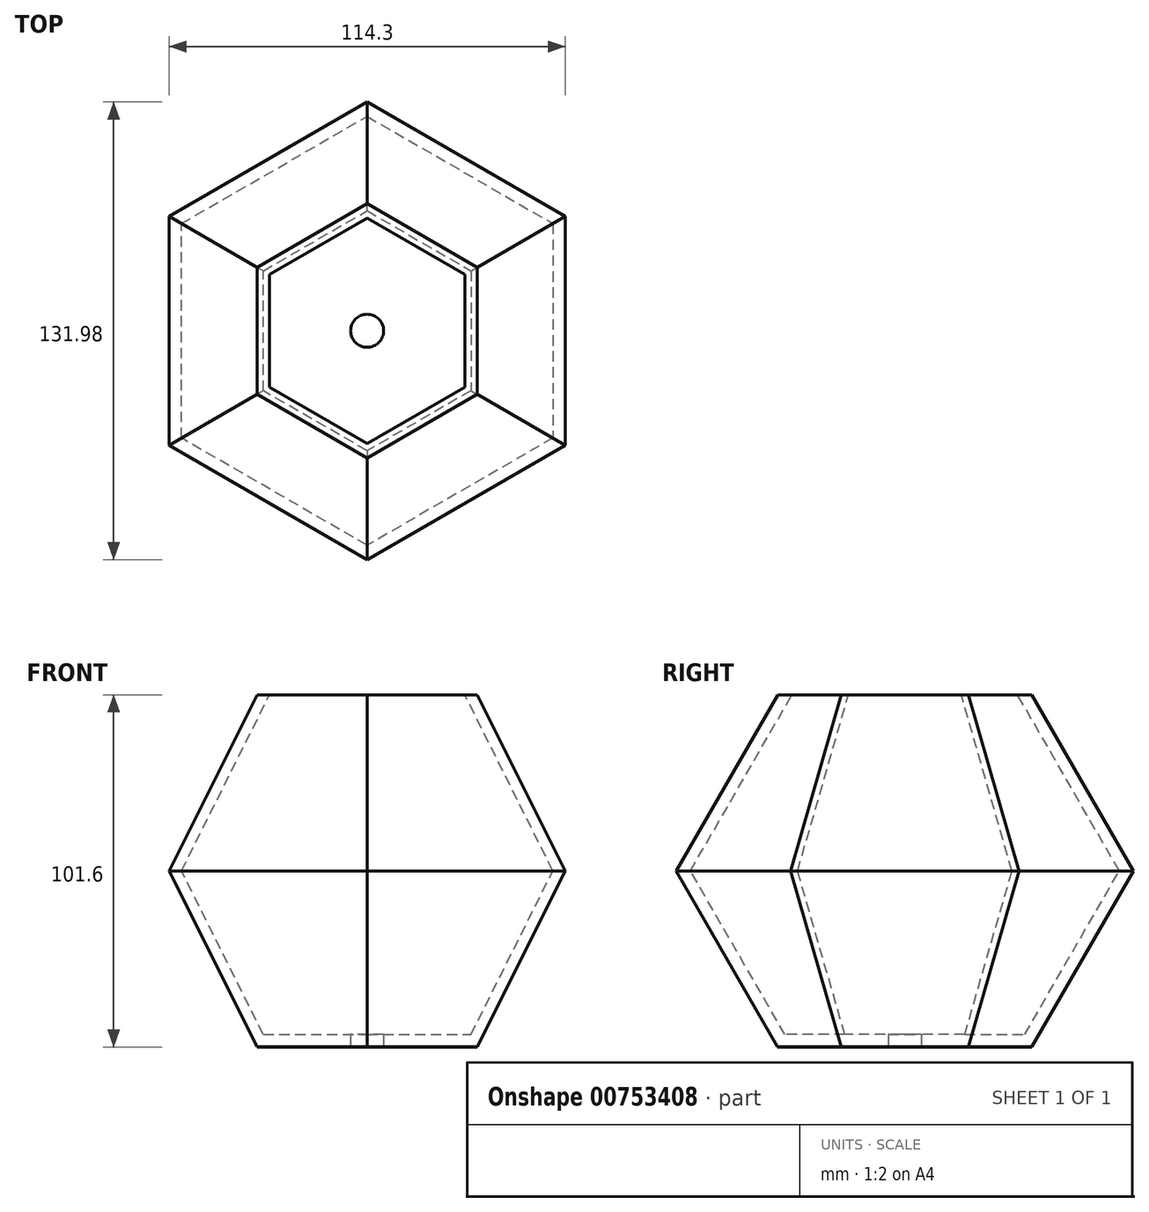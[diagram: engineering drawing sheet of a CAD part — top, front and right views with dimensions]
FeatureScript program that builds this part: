
annotation { "Feature Type Name" : "Feature", "Feature Type Description" : "" }
export const myFeature = defineFeature(function(context is Context, id is Id, definition is map)
    precondition{}
    {
        {
            var Q0;
            Q0=qCreatedBy(makeId("Top.planeOp"),FACE);
            var sketch = newSketch(context, id + "F0", { "sketchPlane" : qUnion([Q0])});
            skCircle(sketch, "E0.cCircle", {"center": v(0, 0) * mm, "radius": 31.75 * mm, "construction": true});
            skLineSegment(sketch, "E0.0", {"start": v(-31.75, -18.33) * mm, "end": v(-31.75, 18.33) * mm});
            skLineSegment(sketch, "E0.1", {"start": v(-31.75, 18.33) * mm, "end": v(0, 36.66) * mm});
            skLineSegment(sketch, "E0.2", {"start": v(0, 36.66) * mm, "end": v(31.75, 18.33) * mm});
            skLineSegment(sketch, "E0.3", {"start": v(31.75, 18.33) * mm, "end": v(31.75, -18.33) * mm});
            skLineSegment(sketch, "E0.4", {"start": v(31.75, -18.33) * mm, "end": v(0, -36.66) * mm});
            skLineSegment(sketch, "E0.5", {"start": v(0, -36.66) * mm, "end": v(-31.75, -18.33) * mm});
            skPoint(sketch, "E0.0.midPoint", {"position": v(-31.75, 0) * mm});
            skSolve(sketch);
        }
        {
            var Q0;
            Q0=qCreatedBy(makeId("Top.planeOp"),FACE);
            cPlane(context, id + "F1", {"entities" : qUnion([Q0]), "cplaneType" : CPlaneType.OFFSET, "offset" : 50.8 * mm, "width" : 152.4 * mm, "height" : 152.4 * mm});
        }
        {
            var Q0;
            Q0=qCreatedBy(id+"F1.planeOp",FACE);
            var sketch = newSketch(context, id + "F2", { "sketchPlane" : qUnion([Q0])});
            skCircle(sketch, "E1.cCircle", {"center": v(0, 0) * mm, "radius": 57.15 * mm, "construction": true});
            skLineSegment(sketch, "E1.0", {"start": v(-57.15, -33) * mm, "end": v(-57.15, 33) * mm});
            skLineSegment(sketch, "E1.1", {"start": v(-57.15, 33) * mm, "end": v(0, 66) * mm});
            skLineSegment(sketch, "E1.2", {"start": v(0, 66) * mm, "end": v(57.15, 33) * mm});
            skLineSegment(sketch, "E1.3", {"start": v(57.15, 33) * mm, "end": v(57.15, -33) * mm});
            skLineSegment(sketch, "E1.4", {"start": v(57.15, -33) * mm, "end": v(0, -66) * mm});
            skLineSegment(sketch, "E1.5", {"start": v(0, -66) * mm, "end": v(-57.15, -33) * mm});
            skPoint(sketch, "E1.0.midPoint", {"position": v(-57.15, 0) * mm});
            skSolve(sketch);
        }
        {
            var Q0;
            Q0=qCreatedBy(makeId("Top.planeOp"),FACE);
            cPlane(context, id + "F3", {"entities" : qUnion([Q0]), "cplaneType" : CPlaneType.OFFSET, "offset" : 101.6 * mm, "width" : 152.4 * mm, "height" : 152.4 * mm});
        }
        {
            var Q0;
            Q0=qCreatedBy(id+"F3.planeOp",FACE);
            var sketch = newSketch(context, id + "F4", { "sketchPlane" : qUnion([Q0])});
            skCircle(sketch, "E2.cCircle", {"center": v(0, 0) * mm, "radius": 31.75 * mm, "construction": true});
            skLineSegment(sketch, "E2.0", {"start": v(-31.75, -18.33) * mm, "end": v(-31.75, 18.33) * mm});
            skLineSegment(sketch, "E2.1", {"start": v(-31.75, 18.33) * mm, "end": v(0, 36.66) * mm});
            skLineSegment(sketch, "E2.2", {"start": v(0, 36.66) * mm, "end": v(31.75, 18.33) * mm});
            skLineSegment(sketch, "E2.3", {"start": v(31.75, 18.33) * mm, "end": v(31.75, -18.33) * mm});
            skLineSegment(sketch, "E2.4", {"start": v(31.75, -18.33) * mm, "end": v(0, -36.66) * mm});
            skLineSegment(sketch, "E2.5", {"start": v(0, -36.66) * mm, "end": v(-31.75, -18.33) * mm});
            skPoint(sketch, "E2.0.midPoint", {"position": v(-31.75, 0) * mm});
            skSolve(sketch);
        }
        {
            var Q0;
            Q0=makeQuery(id+"F0.imprint","IMPRINT",FACE,{"disambiguationData":[TD([[makeQuery(id+"F0.imprint","IMPRINT",EDGE,{"derivedFrom":sQuery(id+"F0.wireOp",EDGE,"E0.0")}),-1.0]])]});
            var Q1;
            Q1=makeQuery(id+"F2.imprint","IMPRINT",FACE,{"disambiguationData":[TD([[makeQuery(id+"F2.imprint","IMPRINT",EDGE,{"derivedFrom":sQuery(id+"F2.wireOp",EDGE,"E1.0")}),-1.0]])]});
            loft(context, id + "F5", {"sheetProfilesArray" : [{ "sheetProfileEntities" : qUnion([Q0]) }, { "sheetProfileEntities" : qUnion([Q1]) }]});
        }
        {
            var Q1;
            Q1=makeQuery(id+"F5.opLoft","CAP_FACE",FACE,{"disambiguationData":[OSD([makeQuery(id+"F2.imprint","IMPRINT",FACE,{"disambiguationData":[TD([[makeQuery(id+"F2.imprint","IMPRINT",EDGE,{"derivedFrom":sQuery(id+"F2.wireOp",EDGE,"E1.0")}),-1.0]])]})])],"isStart":true});
            var Q2;
            Q2=makeQuery(id+"F4.imprint","IMPRINT",FACE,{"disambiguationData":[TD([[makeQuery(id+"F4.imprint","IMPRINT",EDGE,{"derivedFrom":sQuery(id+"F4.wireOp",EDGE,"E2.0")}),-1.0]])]});
            loft(context, id + "F6", {"operationType" : NewBodyOperationType.ADD, "sheetProfilesArray" : [{ "sheetProfileEntities" : qUnion([Q1]) }, { "sheetProfileEntities" : qUnion([Q2]) }]});
        }
        {
            var Q0;
            Q0=makeQuery(id+"F5.opLoft","CAP_FACE",FACE,{"disambiguationData":[OSD([makeQuery(id+"F0.imprint","IMPRINT",FACE,{"disambiguationData":[TD([[makeQuery(id+"F0.imprint","IMPRINT",EDGE,{"derivedFrom":sQuery(id+"F0.wireOp",EDGE,"E0.0")}),-1.0]])]})])],"isStart":true});
            var sketch = newSketch(context, id + "F7", { "sketchPlane" : qUnion([Q0])});
            skCircle(sketch, "E3.cCircle", {"center": v(0, 0) * mm, "radius": 28.18 * mm, "construction": true});
            skLineSegment(sketch, "E3.0", {"start": v(-28.18, -16.27) * mm, "end": v(-28.18, 16.27) * mm});
            skLineSegment(sketch, "E3.1", {"start": v(-28.18, 16.27) * mm, "end": v(0, 32.54) * mm});
            skLineSegment(sketch, "E3.2", {"start": v(0, 32.54) * mm, "end": v(28.18, 16.27) * mm});
            skLineSegment(sketch, "E3.3", {"start": v(28.18, 16.27) * mm, "end": v(28.18, -16.27) * mm});
            skLineSegment(sketch, "E3.4", {"start": v(28.18, -16.27) * mm, "end": v(0, -32.54) * mm});
            skLineSegment(sketch, "E3.5", {"start": v(0, -32.54) * mm, "end": v(-28.18, -16.27) * mm});
            skPoint(sketch, "E3.0.midPoint", {"position": v(-28.18, 0) * mm});
            skSolve(sketch);
        }
        {
            var Q0;
            Q0=qCreatedBy(id+"F1.planeOp",FACE);
            var sketch = newSketch(context, id + "F8", { "sketchPlane" : qUnion([Q0])});
            skCircle(sketch, "E4.cCircle", {"center": v(0, 0) * mm, "radius": 53.58 * mm, "construction": true});
            skLineSegment(sketch, "E4.0", {"start": v(-53.58, -30.93) * mm, "end": v(-53.58, 30.93) * mm});
            skLineSegment(sketch, "E4.1", {"start": v(-53.58, 30.93) * mm, "end": v(0, 61.87) * mm});
            skLineSegment(sketch, "E4.2", {"start": v(0, 61.87) * mm, "end": v(53.58, 30.93) * mm});
            skLineSegment(sketch, "E4.3", {"start": v(53.58, 30.93) * mm, "end": v(53.58, -30.93) * mm});
            skLineSegment(sketch, "E4.4", {"start": v(53.58, -30.93) * mm, "end": v(0, -61.87) * mm});
            skLineSegment(sketch, "E4.5", {"start": v(0, -61.87) * mm, "end": v(-53.58, -30.93) * mm});
            skPoint(sketch, "E4.0.midPoint", {"position": v(-53.58, 0) * mm});
            skSolve(sketch);
        }
        {
            var Q1;
            Q1 = qSketchRegion(id + "F7", true);
            var Q2;
            Q2 = qSketchRegion(id + "F8", true);
            loft(context, id + "F9", {"operationType" : NewBodyOperationType.REMOVE, "sheetProfilesArray" : [{ "sheetProfileEntities" : qUnion([Q1]) }, { "sheetProfileEntities" : qUnion([Q2]) }]});
        }
        {
            var Q0;
            Q0=makeQuery(id+"F6.opLoft","CAP_FACE",FACE,{"disambiguationData":[OSD([makeQuery(id+"F4.imprint","IMPRINT",FACE,{"disambiguationData":[TD([[makeQuery(id+"F4.imprint","IMPRINT",EDGE,{"derivedFrom":sQuery(id+"F4.wireOp",EDGE,"E2.0")}),-1.0]])]})])],"isStart":true});
            var sketch = newSketch(context, id + "F10", { "sketchPlane" : qUnion([Q0])});
            skCircle(sketch, "E5.cCircle", {"center": v(0, 0) * mm, "radius": 28.18 * mm, "construction": true});
            skLineSegment(sketch, "E5.0", {"start": v(-28.18, -16.27) * mm, "end": v(-28.18, 16.27) * mm});
            skLineSegment(sketch, "E5.1", {"start": v(-28.18, 16.27) * mm, "end": v(0, 32.54) * mm});
            skLineSegment(sketch, "E5.2", {"start": v(0, 32.54) * mm, "end": v(28.18, 16.27) * mm});
            skLineSegment(sketch, "E5.3", {"start": v(28.18, 16.27) * mm, "end": v(28.18, -16.27) * mm});
            skLineSegment(sketch, "E5.4", {"start": v(28.18, -16.27) * mm, "end": v(0, -32.54) * mm});
            skLineSegment(sketch, "E5.5", {"start": v(0, -32.54) * mm, "end": v(-28.18, -16.27) * mm});
            skPoint(sketch, "E5.0.midPoint", {"position": v(-28.18, 0) * mm});
            skSolve(sketch);
        }
        {
            var Q1;
            Q1 = qSketchRegion(id + "F8", true);
            var Q2;
            Q2 = qSketchRegion(id + "F10", true);
            loft(context, id + "F11", {"operationType" : NewBodyOperationType.REMOVE, "sheetProfilesArray" : [{ "sheetProfileEntities" : qUnion([Q1]) }, { "sheetProfileEntities" : qUnion([Q2]) }]});
        }
        {
            var Q0;
            Q0=qCreatedBy(makeId("Top.planeOp"),FACE);
            var sketch = newSketch(context, id + "F12", { "sketchPlane" : qUnion([Q0])});
            skCircle(sketch, "E6.cCircle", {"center": v(0, 0) * mm, "radius": 31.78 * mm, "construction": true});
            skLineSegment(sketch, "E6.0", {"start": v(-31.78, -18.35) * mm, "end": v(-31.78, 18.35) * mm});
            skLineSegment(sketch, "E6.1", {"start": v(-31.78, 18.35) * mm, "end": v(0, 36.7) * mm});
            skLineSegment(sketch, "E6.2", {"start": v(0, 36.7) * mm, "end": v(31.78, 18.35) * mm});
            skLineSegment(sketch, "E6.3", {"start": v(31.78, 18.35) * mm, "end": v(31.78, -18.35) * mm});
            skLineSegment(sketch, "E6.4", {"start": v(31.78, -18.35) * mm, "end": v(0, -36.7) * mm});
            skLineSegment(sketch, "E6.5", {"start": v(0, -36.7) * mm, "end": v(-31.78, -18.35) * mm});
            skPoint(sketch, "E6.0.midPoint", {"position": v(-31.78, 0) * mm});
            skCircle(sketch, "E7", {"center": v(0, 0) * mm, "radius": 4.76 * mm});
            skSolve(sketch);
        }
        {
            var Q0;
            Q0 = qSketchRegion(id + "F12", true);
            extrude(context, id + "F13", {"entities" : qUnion([Q0]), "operationType" : NewBodyOperationType.ADD, "depth" : 3.57 * mm, "offsetDistance" : 25.4 * mm});
        }
    });
